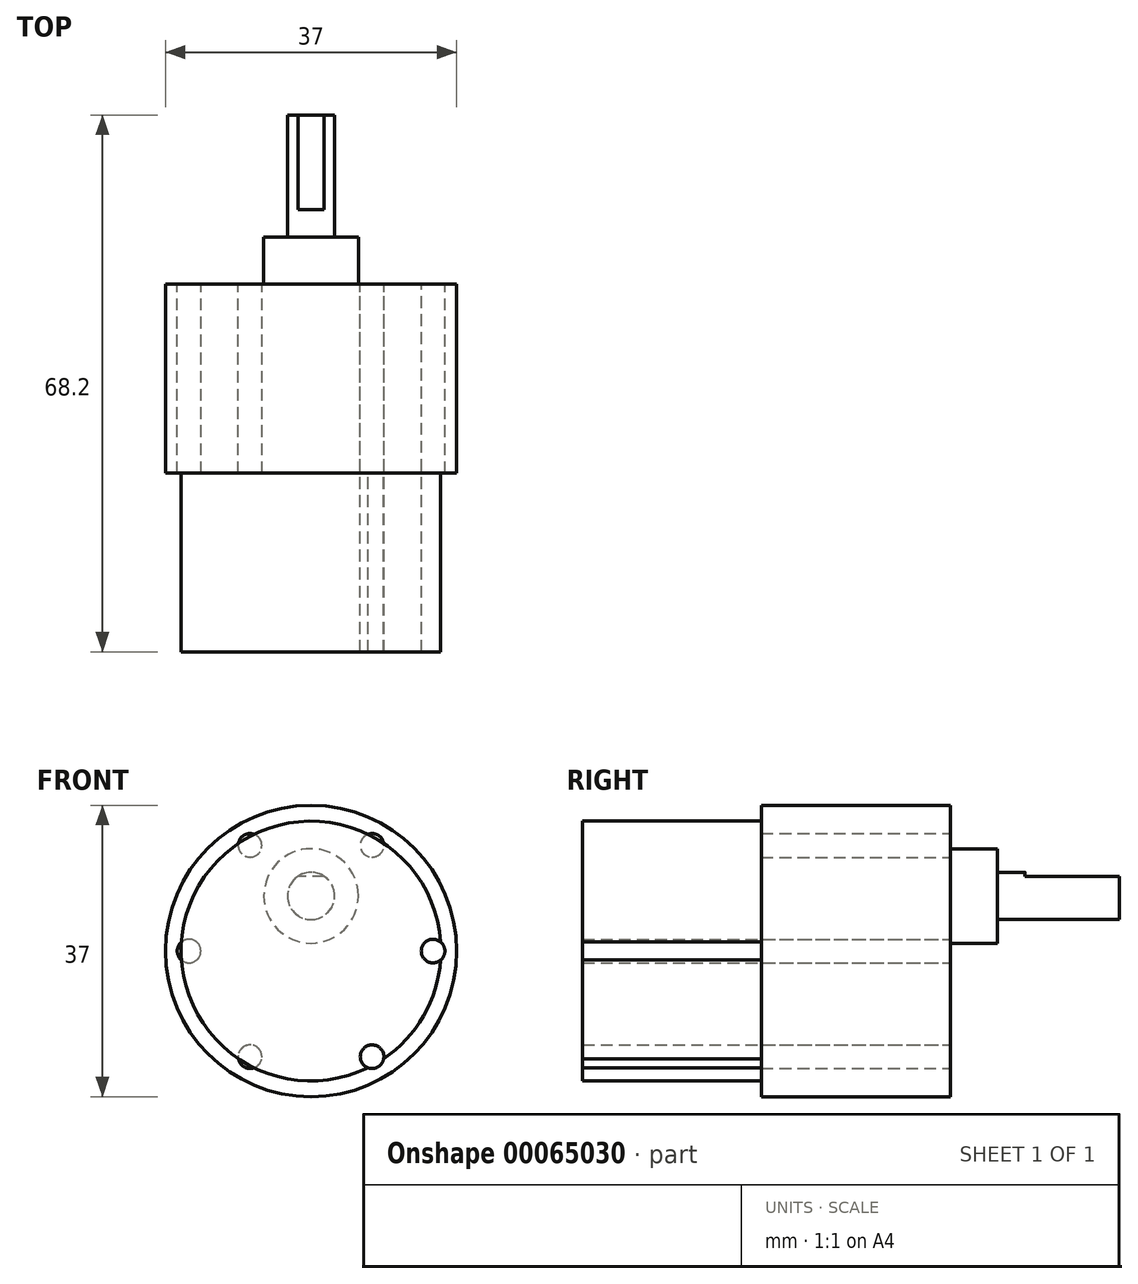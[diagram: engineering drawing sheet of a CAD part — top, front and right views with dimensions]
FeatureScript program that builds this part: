
annotation { "Feature Type Name" : "Feature", "Feature Type Description" : "" }
export const myFeature = defineFeature(function(context is Context, id is Id, definition is map)
    precondition{}
    {
        {
            var Q0;
            Q0=qCreatedBy(makeId("Front.planeOp"),FACE);
            var sketch = newSketch(context, id + "F0", { "sketchPlane" : qUnion([Q0])});
            skCircle(sketch, "E0", {"center": v(0, 0) * mm, "radius": 18.5 * mm});
            skCircle(sketch, "E1", {"center": v(0, 7) * mm, "radius": 3 * mm});
            skCircle(sketch, "E2", {"center": v(0, 7) * mm, "radius": 6 * mm});
            skCircle(sketch, "E3", {"center": v(0, 0) * mm, "radius": 15.5 * mm, "construction": true});
            skCircle(sketch, "E4", {"center": v(15.5, 0) * mm, "radius": 1.5 * mm});
            skCircle(sketch, "E5.1.0", {"center": v(7.75, 13.42) * mm, "radius": 1.5 * mm});
            skCircle(sketch, "E5.2.0", {"center": v(-7.75, 13.42) * mm, "radius": 1.5 * mm});
            skCircle(sketch, "E5.3.0", {"center": v(-15.5, 0) * mm, "radius": 1.5 * mm});
            skCircle(sketch, "E5.4.0", {"center": v(-7.75, -13.42) * mm, "radius": 1.5 * mm});
            skCircle(sketch, "E5.5.0", {"center": v(7.75, -13.42) * mm, "radius": 1.5 * mm});
            skSolve(sketch);
        }
        {
            var Q0;
            Q0=makeQuery(id+"F0.imprint","IMPRINT",FACE,{"disambiguationData":[TD([[makeQuery(id+"F0.imprint","IMPRINT",EDGE,{"derivedFrom":sQuery(id+"F0.wireOp",EDGE,"E0")}),1.0]])]});
            var Q1;
            Q1=makeQuery(id+"F0.imprint","IMPRINT",FACE,{"disambiguationData":[TD([[makeQuery(id+"F0.imprint","IMPRINT",EDGE,{"derivedFrom":sQuery(id+"F0.wireOp",EDGE,"E1")}),-1.0]])]});
            var Q2;
            Q2=makeQuery(id+"F0.imprint","IMPRINT",FACE,{"disambiguationData":[TD([[makeQuery(id+"F0.imprint","IMPRINT",EDGE,{"derivedFrom":sQuery(id+"F0.wireOp",EDGE,"E1")}),1.0]])]});
            extrude(context, id + "F1", {"entities" : qUnion([Q0, Q1, Q2]), "depth" : 24 * mm});
        }
        {
            var Q0;
            Q0=makeQuery(id+"F0.imprint","IMPRINT",FACE,{"disambiguationData":[TD([[makeQuery(id+"F0.imprint","IMPRINT",EDGE,{"derivedFrom":sQuery(id+"F0.wireOp",EDGE,"E1")}),1.0]])]});
            extrude(context, id + "F2", {"entities" : qUnion([Q0]), "operationType" : NewBodyOperationType.ADD, "oppositeDirection" : true, "depth" : (6 + 15.5) * mm});
        }
        {
            var Q0;
            Q0=makeQuery(id+"F0.imprint","IMPRINT",FACE,{"disambiguationData":[TD([[makeQuery(id+"F0.imprint","IMPRINT",EDGE,{"derivedFrom":sQuery(id+"F0.wireOp",EDGE,"E1")}),-1.0]])]});
            extrude(context, id + "F3", {"entities" : qUnion([Q0]), "operationType" : NewBodyOperationType.ADD, "oppositeDirection" : true, "depth" : 6 * mm});
        }
        {
            var Q0;
            Q0=makeQuery(id+"F2.opExtrude","CAP_FACE",FACE,{"disambiguationData":[OSD([sQuery(id+"F0.wireOp",EDGE,"E1")])],"isStart":false});
            var sketch = newSketch(context, id + "F4", { "sketchPlane" : qUnion([Q0])});
            skLineSegment(sketch, "E6", {"start": v(0, 7) * mm, "end": v(0, 10.7) * mm, "construction": true});
            skLineSegment(sketch, "E7.bottom", {"start": v(-2, 9.5) * mm, "end": v(2, 9.5) * mm});
            skLineSegment(sketch, "E7.top", {"start": v(-2, 10.5) * mm, "end": v(2, 10.5) * mm});
            skLineSegment(sketch, "E7.left", {"start": v(-2, 9.5) * mm, "end": v(-2, 10.5) * mm});
            skLineSegment(sketch, "E7.right", {"start": v(2, 9.5) * mm, "end": v(2, 10.5) * mm});
            skSolve(sketch);
        }
        {
            var Q0;
            {var subQ0=sQuery(id+"F4.wireOp",EDGE,"E7.bottom");var subQ1=makeQuery(id+"F2.opExtrude","CAP_EDGE",EDGE,{"disambiguationData":[OSD([sQuery(id+"F0.wireOp",EDGE,"E1")])],"isStart":false});var subQ2=makeQuery(id+"F4.imprint","INTERSECT",VERTEX,{"disambiguationData":[OD(0.0)],"derivedFrom":[subQ1,subQ0]});Q0=makeQuery(id+"F4.imprint","IMPRINT",FACE,{"disambiguationData":[TD([[makeQuery(id+"F4.imprint","IMPRINT",EDGE,{"disambiguationData":[TD([[subQ2,-1.0]])],"derivedFrom":subQ0}),1.0]])]});}
            var Q1;
            Q1=makeQuery(id+"F4.imprint","IMPRINT",FACE,{"disambiguationData":[TD([[makeQuery(id+"F4.imprint","IMPRINT",EDGE,{"derivedFrom":sQuery(id+"F4.wireOp",EDGE,"E7.top")}),-1.0]])]});
            extrude(context, id + "F5", {"entities" : qUnion([Q0, Q1]), "operationType" : NewBodyOperationType.REMOVE, "oppositeDirection" : true, "depth" : 12 * mm});
        }
        {
            var Q0;
            Q0=makeQuery(id+"F1.opExtrude","CAP_FACE",FACE,{"disambiguationData":[OSD([sQuery(id+"F0.wireOp",EDGE,"E0")])],"isStart":false});
            var sketch = newSketch(context, id + "F6", { "sketchPlane" : qUnion([Q0])});
            skCircle(sketch, "E8", {"center": v(0, 0) * mm, "radius": 16.5 * mm});
            skSolve(sketch);
        }
        {
            var Q0;
            {var subQ0=sQuery(id+"F6.wireOp",EDGE,"E8");var subQ1=makeQuery(id+"F1.opExtrude","CAP_EDGE",EDGE,{"disambiguationData":[OSD([sQuery(id+"F0.wireOp",EDGE,"E5.1.0")])],"isStart":false});var subQ2=makeQuery(id+"F6.imprint","INTERSECT",VERTEX,{"disambiguationData":[OD(0.0)],"derivedFrom":[subQ1,subQ0]});Q0=makeQuery(id+"F6.imprint","IMPRINT",FACE,{"disambiguationData":[TD([[makeQuery(id+"F6.imprint","IMPRINT",EDGE,{"disambiguationData":[TD([[subQ2,1.0]])],"derivedFrom":subQ0}),1.0]])]});}
            var Q1;
            {var subQ0=sQuery(id+"F6.wireOp",EDGE,"E8");var subQ1=makeQuery(id+"F1.opExtrude","CAP_EDGE",EDGE,{"disambiguationData":[OSD([sQuery(id+"F0.wireOp",EDGE,"E5.1.0")])],"isStart":false});var subQ2=makeQuery(id+"F6.imprint","INTERSECT",VERTEX,{"disambiguationData":[OD(0.0)],"derivedFrom":[subQ1,subQ0]});Q1=makeQuery(id+"F6.imprint","IMPRINT",FACE,{"disambiguationData":[TD([[makeQuery(id+"F6.imprint","IMPRINT",EDGE,{"disambiguationData":[TD([[subQ2,-1.0]])],"derivedFrom":subQ0}),1.0]])]});}
            var Q2;
            {var subQ0=sQuery(id+"F6.wireOp",EDGE,"E8");var subQ1=makeQuery(id+"F1.opExtrude","CAP_EDGE",EDGE,{"disambiguationData":[OSD([sQuery(id+"F0.wireOp",EDGE,"E5.2.0")])],"isStart":false});var subQ2=makeQuery(id+"F6.imprint","INTERSECT",VERTEX,{"disambiguationData":[OD(0.0)],"derivedFrom":[subQ1,subQ0]});Q2=makeQuery(id+"F6.imprint","IMPRINT",FACE,{"disambiguationData":[TD([[makeQuery(id+"F6.imprint","IMPRINT",EDGE,{"disambiguationData":[TD([[subQ2,-1.0]])],"derivedFrom":subQ0}),1.0]])]});}
            var Q3;
            {var subQ0=sQuery(id+"F6.wireOp",EDGE,"E8");var subQ1=makeQuery(id+"F1.opExtrude","CAP_EDGE",EDGE,{"disambiguationData":[OSD([sQuery(id+"F0.wireOp",EDGE,"E4")])],"isStart":false});var subQ2=makeQuery(id+"F6.imprint","INTERSECT",VERTEX,{"disambiguationData":[OD(0.0)],"derivedFrom":[subQ1,subQ0]});Q3=makeQuery(id+"F6.imprint","IMPRINT",FACE,{"disambiguationData":[TD([[makeQuery(id+"F6.imprint","IMPRINT",EDGE,{"disambiguationData":[TD([[subQ2,1.0]])],"derivedFrom":subQ0}),1.0]])]});}
            var Q4;
            {var subQ0=sQuery(id+"F6.wireOp",EDGE,"E8");var subQ1=makeQuery(id+"F1.opExtrude","CAP_EDGE",EDGE,{"disambiguationData":[OSD([sQuery(id+"F0.wireOp",EDGE,"E5.3.0")])],"isStart":false});var subQ2=makeQuery(id+"F6.imprint","INTERSECT",VERTEX,{"disambiguationData":[OD(0.0)],"derivedFrom":[subQ1,subQ0]});Q4=makeQuery(id+"F6.imprint","IMPRINT",FACE,{"disambiguationData":[TD([[makeQuery(id+"F6.imprint","IMPRINT",EDGE,{"disambiguationData":[TD([[subQ2,-1.0]])],"derivedFrom":subQ0}),1.0]])]});}
            var Q5;
            {var subQ0=sQuery(id+"F6.wireOp",EDGE,"E8");var subQ1=makeQuery(id+"F1.opExtrude","CAP_EDGE",EDGE,{"disambiguationData":[OSD([sQuery(id+"F0.wireOp",EDGE,"E5.4.0")])],"isStart":false});var subQ2=makeQuery(id+"F6.imprint","INTERSECT",VERTEX,{"disambiguationData":[OD(0.0)],"derivedFrom":[subQ1,subQ0]});Q5=makeQuery(id+"F6.imprint","IMPRINT",FACE,{"disambiguationData":[TD([[makeQuery(id+"F6.imprint","IMPRINT",EDGE,{"disambiguationData":[TD([[subQ2,-1.0]])],"derivedFrom":subQ0}),1.0]])]});}
            var Q6;
            {var subQ0=sQuery(id+"F6.wireOp",EDGE,"E8");var subQ1=makeQuery(id+"F1.opExtrude","CAP_EDGE",EDGE,{"disambiguationData":[OSD([sQuery(id+"F0.wireOp",EDGE,"E5.5.0")])],"isStart":false});var subQ2=makeQuery(id+"F6.imprint","INTERSECT",VERTEX,{"disambiguationData":[OD(0.0)],"derivedFrom":[subQ1,subQ0]});Q6=makeQuery(id+"F6.imprint","IMPRINT",FACE,{"disambiguationData":[TD([[makeQuery(id+"F6.imprint","IMPRINT",EDGE,{"disambiguationData":[TD([[subQ2,-1.0]])],"derivedFrom":subQ0}),1.0]])]});}
            extrude(context, id + "F7", {"entities" : qUnion([Q0, Q1, Q2, Q3, Q4, Q5, Q6]), "operationType" : NewBodyOperationType.ADD, "depth" : 22.7 * mm});
        }
    });
